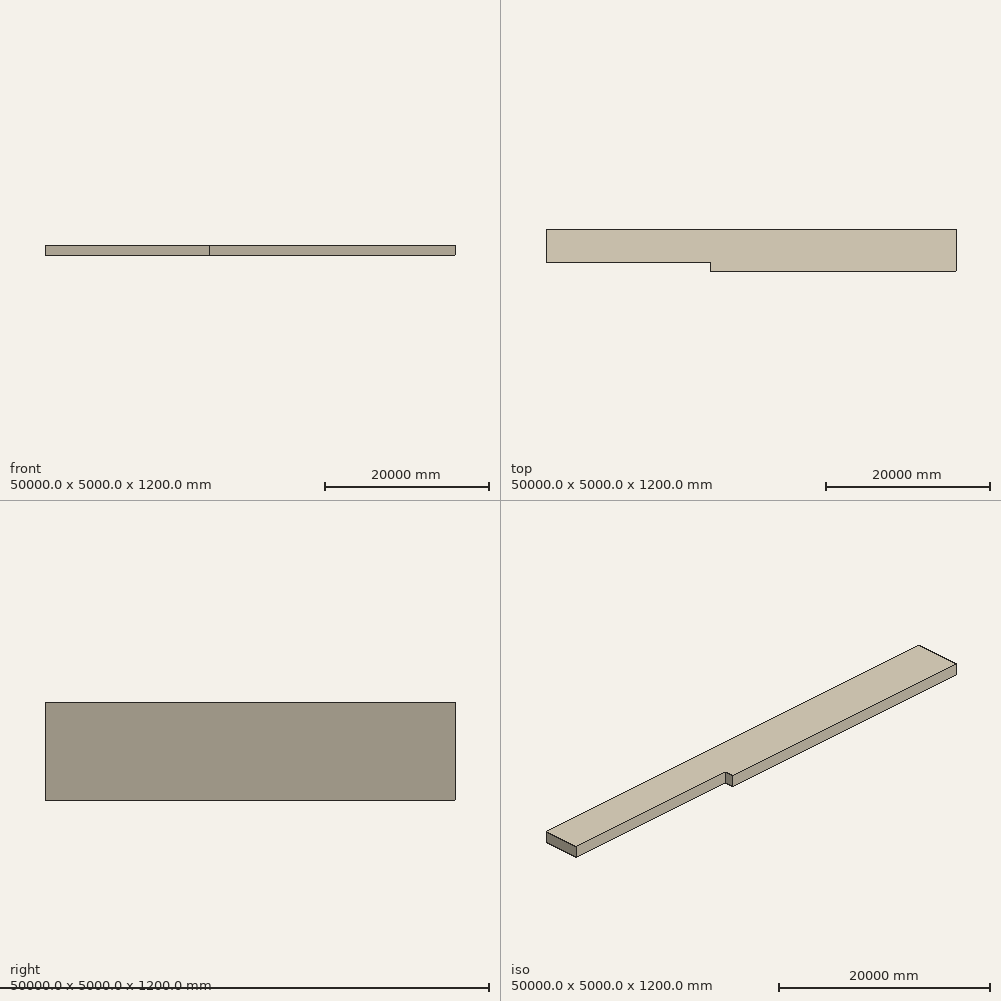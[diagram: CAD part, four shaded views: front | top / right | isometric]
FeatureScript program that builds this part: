
annotation { "Feature Type Name" : "Feature", "Feature Type Description" : "" }
export const myFeature = defineFeature(function(context is Context, id is Id, definition is map)
    precondition{}
    {
        {
            var Q0;
            Q0=qCreatedBy(makeId("Front.planeOp"),FACE);
            var sketch = newSketch(context, id + "F0", { "sketchPlane" : qUnion([Q0])});
            skLineSegment(sketch, "E0.bottom", {"start": v(25000, 600) * mm, "end": v(-25000, 600) * mm});
            skLineSegment(sketch, "E0.top", {"start": v(25000, -600) * mm, "end": v(-25000, -600) * mm});
            skLineSegment(sketch, "E0.left", {"start": v(25000, 600) * mm, "end": v(25000, -600) * mm});
            skLineSegment(sketch, "E0.right", {"start": v(-25000, 600) * mm, "end": v(-25000, -600) * mm});
            skPoint(sketch, "E0.middle", {"position": v(0, 0) * mm});
            skSolve(sketch);
        }
        {
            var Q0;
            Q0 = qSketchRegion(id + "F0", true);
            extrude(context, id + "F1", {"entities" : qUnion([Q0]), "oppositeDirection" : true, "depth" : 4000 * mm});
        }
        {
            var Q0;
            Q0=makeQuery(id+"F0.imprint","IMPRINT",FACE,{"disambiguationData":[TD([[makeQuery(id+"F0.imprint","IMPRINT",EDGE,{"derivedFrom":sQuery(id+"F0.wireOp",EDGE,"E0.bottom")}),1.0]])]});
            var sketch = newSketch(context, id + "F2", { "sketchPlane" : qUnion([Q0])});
            skPoint(sketch, "E1", {"position": v(-15000, 0) * mm});
            skPoint(sketch, "E2", {"position": v(25000, 600) * mm});
            skPoint(sketch, "E3", {"position": v(-4400, -600) * mm});
            skPoint(sketch, "E4", {"position": v(-5000, -600) * mm});
            skLineSegment(sketch, "E5.bottom", {"start": v(25000, 600) * mm, "end": v(-5000, 600) * mm});
            skLineSegment(sketch, "E5.top", {"start": v(25000, -600) * mm, "end": v(-5000, -600) * mm});
            skLineSegment(sketch, "E5.left", {"start": v(25000, 600) * mm, "end": v(25000, -600) * mm});
            skLineSegment(sketch, "E5.right", {"start": v(-5000, 600) * mm, "end": v(-5000, -600) * mm});
            skSolve(sketch);
        }
        {
            var Q0;
            Q0 = qSketchRegion(id + "F2", true);
            extrude(context, id + "F3", {"entities" : qUnion([Q0]), "operationType" : NewBodyOperationType.ADD, "depth" : 1000 * mm});
        }
    });
